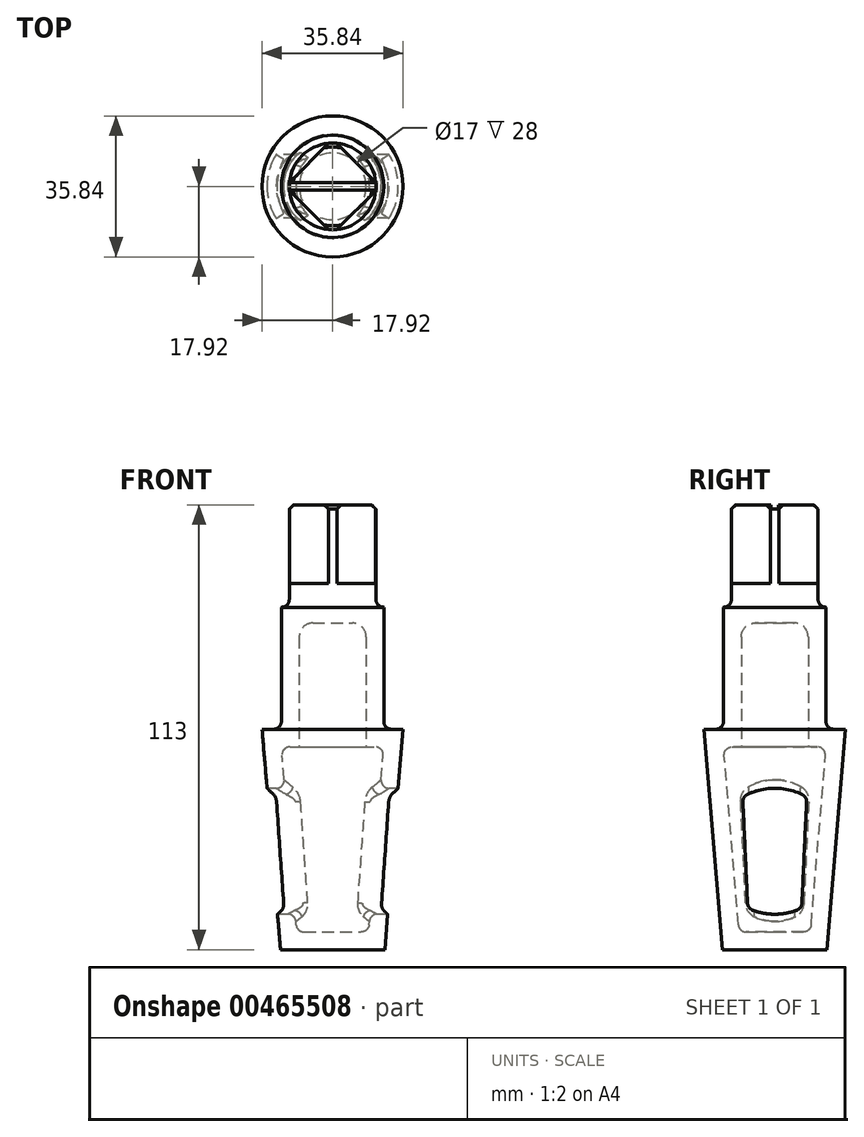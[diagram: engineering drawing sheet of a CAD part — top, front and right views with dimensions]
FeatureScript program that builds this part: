
annotation { "Feature Type Name" : "Feature", "Feature Type Description" : "" }
export const myFeature = defineFeature(function(context is Context, id is Id, definition is map)
    precondition{}
    {
        {
            var Q0;
            Q0=qCreatedBy(makeId("Front.planeOp"),FACE);
            var sketch = newSketch(context, id + "F0", { "sketchPlane" : qUnion([Q0])});
            skLineSegment(sketch, "E0", {"start": v(0, -32.47) * mm, "end": v(0, 104.3) * mm, "construction": true});
            skLineSegment(sketch, "E1", {"start": v(0, -25) * mm, "end": v(13.25, -25) * mm});
            skLineSegment(sketch, "E2", {"start": v(13.25, -25) * mm, "end": v(17.92, 31) * mm});
            skLineSegment(sketch, "E3", {"start": v(17.92, 31) * mm, "end": v(13, 31) * mm});
            skLineSegment(sketch, "E4", {"start": v(13, 31) * mm, "end": v(13, 62) * mm});
            skLineSegment(sketch, "E5", {"start": v(13, 62) * mm, "end": v(11, 62) * mm});
            skLineSegment(sketch, "E6", {"start": v(11, 62) * mm, "end": v(11, 88) * mm});
            skLineSegment(sketch, "E7", {"start": v(11, 88) * mm, "end": v(0, 88) * mm});
            skLineSegment(sketch, "E8", {"start": v(0, 88) * mm, "end": v(0, -25) * mm});
            skLineSegment(sketch, "E9.0", {"start": v(8.5, 26.5) * mm, "end": v(8.5, 54.5) * mm});
            skLineSegment(sketch, "E9.1", {"start": v(10.85, 26.5) * mm, "end": v(8.5, 26.5) * mm});
            skLineSegment(sketch, "E9.2", {"start": v(9.26, -18.67) * mm, "end": v(12.85, 24.33) * mm});
            skLineSegment(sketch, "E9.3", {"start": v(0, -20.5) * mm, "end": v(7.27, -20.5) * mm});
            skLineSegment(sketch, "E10", {"start": v(0, 58) * mm, "end": v(5, 58) * mm});
            skPoint(sketch, "E11.visualSharp", {"position": v(8.5, 58) * mm});
            skArc(sketch, "E11.filletArc", {"start": v(8.5, 54.5) * mm, "mid": v(7.47, 56.97) * mm, "end": v(5, 58) * mm});
            skPoint(sketch, "E12.visualSharp", {"position": v(13.03, 26.5) * mm});
            skArc(sketch, "E12.filletArc", {"start": v(12.85, 24.33) * mm, "mid": v(12.32, 25.85) * mm, "end": v(10.85, 26.5) * mm});
            skPoint(sketch, "E13.visualSharp", {"position": v(9.1, -20.5) * mm});
            skArc(sketch, "E13.filletArc", {"start": v(7.27, -20.5) * mm, "mid": v(8.62, -19.97) * mm, "end": v(9.26, -18.67) * mm});
            skSolve(sketch);
        }
        {
            var Q0;
            {var subQ1=sQuery(id+"F0.wireOp",EDGE,"E1");Q0=makeQuery(id+"F0.imprint","IMPRINT",FACE,{"disambiguationData":[TD([[makeQuery(id+"F0.imprint","IMPRINT",EDGE,{"derivedFrom":subQ1}),1.0]])]});}
            var Q1;
            Q1=sQuery(id+"F0.wireOp",EDGE,"E0");
            revolve(context, id + "F1", {"entities" : qUnion([Q0]), "axis" : qUnion([Q1]), "revolveType" : RevolveType.FULL});
        }
        {
            var Q0;
            Q0=qCreatedBy(makeId("Right.planeOp"),FACE);
            var sketch = newSketch(context, id + "F2", { "sketchPlane" : qUnion([Q0])});
            skArc(sketch, "E14", {"start": v(6.96, 14.4) * mm, "mid": v(0, 16) * mm, "end": v(-6.96, 14.4) * mm});
            skLineSegment(sketch, "E15", {"start": v(0, 0) * mm, "end": v(0, -8.72) * mm, "construction": true});
            skLineSegment(sketch, "E16", {"start": v(8.1, 12.51) * mm, "end": v(6.9, -13.2) * mm});
            skLineSegment(sketch, "E17.MirrorCS", {"start": v(-8.1, 12.51) * mm, "end": v(-6.9, -13.2) * mm});
            skPoint(sketch, "E18.orphan", {"position": v(8.34, 17.9) * mm});
            skPoint(sketch, "E19.orphan", {"position": v(-8.34, 17.9) * mm});
            skPoint(sketch, "E20.orphan", {"position": v(-6.6, -19.71) * mm});
            skPoint(sketch, "E21.orphan", {"position": v(6.6, -19.71) * mm});
            skArc(sketch, "E22.trimOffspring", {"start": v(-5.61, -14.98) * mm, "mid": v(0, -16) * mm, "end": v(5.61, -14.98) * mm});
            skPoint(sketch, "E23.visualSharp", {"position": v(8.15, 13.77) * mm});
            skArc(sketch, "E23.filletArc", {"start": v(8.1, 12.51) * mm, "mid": v(7.81, 13.63) * mm, "end": v(6.96, 14.4) * mm});
            skPoint(sketch, "E24.visualSharp", {"position": v(-8.15, 13.77) * mm});
            skArc(sketch, "E24.filletArc", {"start": v(-6.96, 14.4) * mm, "mid": v(-7.81, 13.63) * mm, "end": v(-8.1, 12.51) * mm});
            skPoint(sketch, "E25.visualSharp", {"position": v(-6.85, -14.46) * mm});
            skArc(sketch, "E25.filletArc", {"start": v(-6.9, -13.2) * mm, "mid": v(-6.53, -14.29) * mm, "end": v(-5.61, -14.98) * mm});
            skPoint(sketch, "E26.visualSharp", {"position": v(6.85, -14.46) * mm});
            skArc(sketch, "E26.filletArc", {"start": v(5.61, -14.98) * mm, "mid": v(6.53, -14.29) * mm, "end": v(6.9, -13.2) * mm});
            skSolve(sketch);
        }
        {
            var Q0;
            Q0 = qSketchRegion(id + "F2", true);
            extrude(context, id + "F3", {"entities" : qUnion([Q0]), "operationType" : NewBodyOperationType.REMOVE, "depth" : 40 * mm, "symmetric" : true});
        }
        {
            var Q0;
            Q0=makeQuery(id+"F1.opRevolve","SWEPT_EDGE",EDGE,{"disambiguationData":[OSD([sQuery(id+"F0.wireOp",EDGE,"E6"),sQuery(id+"F0.wireOp",EDGE,"E7")])]});
            chamfer(context, id + "F4", {"entities" : qUnion([Q0]), "width" : 1 * mm, "tangentPropagation" : true});
        }
        {
            var Q0;
            Q0=makeQuery(id+"F1.opRevolve","SWEPT_FACE",FACE,{"disambiguationData":[OSD([sQuery(id+"F0.wireOp",EDGE,"E7")])]});
            var sketch = newSketch(context, id + "F5", { "sketchPlane" : qUnion([Q0])});
            skCircle(sketch, "E27.cCircle", {"center": v(0, 0) * mm, "radius": 12.02 * mm, "construction": true});
            skLineSegment(sketch, "E27.0", {"start": v(0, 12.02) * mm, "end": v(12.02, 0) * mm});
            skLineSegment(sketch, "E27.1", {"start": v(12.02, 0) * mm, "end": v(0, -12.02) * mm});
            skLineSegment(sketch, "E27.2", {"start": v(0, -12.02) * mm, "end": v(-12.02, 0) * mm});
            skLineSegment(sketch, "E27.3", {"start": v(-12.02, 0) * mm, "end": v(0, 12.02) * mm});
            skCircle(sketch, "E28.0", {"center": v(0, 0) * mm, "radius": 11 * mm});
            skSolve(sketch);
        }
        {
            var Q0;
            {var subQ0=sQuery(id+"F5.wireOp",EDGE,"E27.3");var subQ1=sQuery(id+"F0.wireOp",EDGE,"E7");var subQ2=makeQuery(id+"F4.opChamfer","BLEND_EDGE",EDGE,{"blendedFrom":[makeQuery(id+"F1.opRevolve","SWEPT_EDGE",EDGE,{"disambiguationData":[OSD([sQuery(id+"F0.wireOp",EDGE,"E6"),subQ1])]}),makeQuery(id+"F1.opRevolve","SWEPT_FACE",FACE,{"disambiguationData":[OSD([subQ1])]})],"blendedInto":[makeQuery(id+"F1.opRevolve","SWEPT_FACE",FACE,{"disambiguationData":[OSD([subQ1])]})]});var subQ3=makeQuery(id+"F5.imprint","INTERSECT",VERTEX,{"disambiguationData":[OD(0.0)],"derivedFrom":[subQ2,subQ0]});Q0=makeQuery(id+"F5.imprint","IMPRINT",FACE,{"disambiguationData":[TD([[makeQuery(id+"F5.imprint","IMPRINT",EDGE,{"disambiguationData":[TD([[subQ3,-1.0]])],"derivedFrom":subQ0}),1.0]])]});}
            var Q1;
            {var subQ0=sQuery(id+"F5.wireOp",EDGE,"E28.0");var subQ1=sQuery(id+"F5.wireOp",EDGE,"E27.3");var subQ2=makeQuery(id+"F5.imprint","INTERSECT",VERTEX,{"disambiguationData":[OD(0.0)],"derivedFrom":[subQ1,subQ0]});Q1=makeQuery(id+"F5.imprint","IMPRINT",FACE,{"disambiguationData":[TD([[makeQuery(id+"F5.imprint","IMPRINT",EDGE,{"disambiguationData":[TD([[subQ2,1.0]])],"derivedFrom":subQ0}),1.0]])]});}
            var Q2;
            {var subQ0=sQuery(id+"F5.wireOp",EDGE,"E27.2");var subQ1=sQuery(id+"F0.wireOp",EDGE,"E7");var subQ2=makeQuery(id+"F4.opChamfer","BLEND_EDGE",EDGE,{"blendedFrom":[makeQuery(id+"F1.opRevolve","SWEPT_EDGE",EDGE,{"disambiguationData":[OSD([sQuery(id+"F0.wireOp",EDGE,"E6"),subQ1])]}),makeQuery(id+"F1.opRevolve","SWEPT_FACE",FACE,{"disambiguationData":[OSD([subQ1])]})],"blendedInto":[makeQuery(id+"F1.opRevolve","SWEPT_FACE",FACE,{"disambiguationData":[OSD([subQ1])]})]});var subQ3=makeQuery(id+"F5.imprint","INTERSECT",VERTEX,{"disambiguationData":[OD(0.0)],"derivedFrom":[subQ2,subQ0]});Q2=makeQuery(id+"F5.imprint","IMPRINT",FACE,{"disambiguationData":[TD([[makeQuery(id+"F5.imprint","IMPRINT",EDGE,{"disambiguationData":[TD([[subQ3,-1.0]])],"derivedFrom":subQ0}),1.0]])]});}
            var Q3;
            {var subQ0=sQuery(id+"F5.wireOp",EDGE,"E28.0");var subQ1=sQuery(id+"F5.wireOp",EDGE,"E27.2");var subQ2=makeQuery(id+"F5.imprint","INTERSECT",VERTEX,{"disambiguationData":[OD(0.0)],"derivedFrom":[subQ1,subQ0]});Q3=makeQuery(id+"F5.imprint","IMPRINT",FACE,{"disambiguationData":[TD([[makeQuery(id+"F5.imprint","IMPRINT",EDGE,{"disambiguationData":[TD([[subQ2,1.0]])],"derivedFrom":subQ0}),1.0]])]});}
            var Q4;
            {var subQ0=sQuery(id+"F5.wireOp",EDGE,"E28.0");var subQ1=sQuery(id+"F5.wireOp",EDGE,"E27.1");var subQ2=makeQuery(id+"F5.imprint","INTERSECT",VERTEX,{"disambiguationData":[OD(0.0)],"derivedFrom":[subQ1,subQ0]});Q4=makeQuery(id+"F5.imprint","IMPRINT",FACE,{"disambiguationData":[TD([[makeQuery(id+"F5.imprint","IMPRINT",EDGE,{"disambiguationData":[TD([[subQ2,1.0]])],"derivedFrom":subQ0}),1.0]])]});}
            var Q5;
            {var subQ0=sQuery(id+"F5.wireOp",EDGE,"E27.1");var subQ1=sQuery(id+"F0.wireOp",EDGE,"E7");var subQ2=makeQuery(id+"F4.opChamfer","BLEND_EDGE",EDGE,{"blendedFrom":[makeQuery(id+"F1.opRevolve","SWEPT_EDGE",EDGE,{"disambiguationData":[OSD([sQuery(id+"F0.wireOp",EDGE,"E6"),subQ1])]}),makeQuery(id+"F1.opRevolve","SWEPT_FACE",FACE,{"disambiguationData":[OSD([subQ1])]})],"blendedInto":[makeQuery(id+"F1.opRevolve","SWEPT_FACE",FACE,{"disambiguationData":[OSD([subQ1])]})]});var subQ3=makeQuery(id+"F5.imprint","INTERSECT",VERTEX,{"disambiguationData":[OD(0.0)],"derivedFrom":[subQ2,subQ0]});Q5=makeQuery(id+"F5.imprint","IMPRINT",FACE,{"disambiguationData":[TD([[makeQuery(id+"F5.imprint","IMPRINT",EDGE,{"disambiguationData":[TD([[subQ3,-1.0]])],"derivedFrom":subQ0}),1.0]])]});}
            var Q6;
            {var subQ0=sQuery(id+"F5.wireOp",EDGE,"E27.0");var subQ1=sQuery(id+"F0.wireOp",EDGE,"E7");var subQ2=makeQuery(id+"F4.opChamfer","BLEND_EDGE",EDGE,{"blendedFrom":[makeQuery(id+"F1.opRevolve","SWEPT_EDGE",EDGE,{"disambiguationData":[OSD([sQuery(id+"F0.wireOp",EDGE,"E6"),subQ1])]}),makeQuery(id+"F1.opRevolve","SWEPT_FACE",FACE,{"disambiguationData":[OSD([subQ1])]})],"blendedInto":[makeQuery(id+"F1.opRevolve","SWEPT_FACE",FACE,{"disambiguationData":[OSD([subQ1])]})]});var subQ3=makeQuery(id+"F5.imprint","INTERSECT",VERTEX,{"disambiguationData":[OD(0.0)],"derivedFrom":[subQ2,subQ0]});Q6=makeQuery(id+"F5.imprint","IMPRINT",FACE,{"disambiguationData":[TD([[makeQuery(id+"F5.imprint","IMPRINT",EDGE,{"disambiguationData":[TD([[subQ3,-1.0]])],"derivedFrom":subQ0}),1.0]])]});}
            var Q7;
            {var subQ0=sQuery(id+"F5.wireOp",EDGE,"E28.0");var subQ1=sQuery(id+"F5.wireOp",EDGE,"E27.0");var subQ2=makeQuery(id+"F5.imprint","INTERSECT",VERTEX,{"disambiguationData":[OD(0.0)],"derivedFrom":[subQ1,subQ0]});Q7=makeQuery(id+"F5.imprint","IMPRINT",FACE,{"disambiguationData":[TD([[makeQuery(id+"F5.imprint","IMPRINT",EDGE,{"disambiguationData":[TD([[subQ2,1.0]])],"derivedFrom":subQ0}),1.0]])]});}
            extrude(context, id + "F6", {"entities" : qUnion([Q0, Q1, Q2, Q3, Q4, Q5, Q6, Q7]), "operationType" : NewBodyOperationType.REMOVE, "oppositeDirection" : true, "depth" : 20 * mm});
        }
        {
            var Q0;
            Q0=makeQuery(id+"F1.opRevolve","SWEPT_FACE",FACE,{"disambiguationData":[OSD([sQuery(id+"F0.wireOp",EDGE,"E7")])]});
            var sketch = newSketch(context, id + "F7", { "sketchPlane" : qUnion([Q0])});
            skLineSegment(sketch, "E29.bottom", {"start": v(-12.5, 1) * mm, "end": v(12.5, 1) * mm});
            skLineSegment(sketch, "E29.top", {"start": v(-12.5, -1) * mm, "end": v(12.5, -1) * mm});
            skLineSegment(sketch, "E29.left", {"start": v(-12.5, 1) * mm, "end": v(-12.5, -1) * mm});
            skLineSegment(sketch, "E29.right", {"start": v(12.5, 1) * mm, "end": v(12.5, -1) * mm});
            skPoint(sketch, "E29.middle", {"position": v(0, 0) * mm});
            skSolve(sketch);
        }
        {
            var Q0;
            Q0 = qSketchRegion(id + "F7", true);
            extrude(context, id + "F8", {"entities" : qUnion([Q0]), "operationType" : NewBodyOperationType.REMOVE, "oppositeDirection" : true, "depth" : 1 * mm});
        }
        {
            var Q0;
            Q0=makeQuery(id+"F1.opRevolve","SWEPT_EDGE",EDGE,{"disambiguationData":[OSD([sQuery(id+"F0.wireOp",EDGE,"E5"),sQuery(id+"F0.wireOp",EDGE,"E6")])]});
            var Q1;
            Q1=makeQuery(id+"F1.opRevolve","SWEPT_EDGE",EDGE,{"disambiguationData":[OSD([sQuery(id+"F0.wireOp",EDGE,"E3"),sQuery(id+"F0.wireOp",EDGE,"E4")])]});
            var Q2;
            Q2=makeQuery(id+"F3.boolean.opBoolean","INTERSECT",EDGE,{"disambiguationData":[OD(0.0)],"derivedFrom":[makeQuery(id+"F1.opRevolve","SWEPT_FACE",FACE,{"disambiguationData":[OSD([sQuery(id+"F0.wireOp",EDGE,"E9.2")])]}),makeQuery(id+"F3.opExtrude","SWEPT_FACE",FACE,{"disambiguationData":[OSD([sQuery(id+"F2.wireOp",EDGE,"E16")])]})]});
            var Q3;
            Q3=makeQuery(id+"F3.boolean.opBoolean","INTERSECT",EDGE,{"disambiguationData":[OD(1.0)],"derivedFrom":[makeQuery(id+"F1.opRevolve","SWEPT_FACE",FACE,{"disambiguationData":[OSD([sQuery(id+"F0.wireOp",EDGE,"E9.2")])]}),makeQuery(id+"F3.opExtrude","SWEPT_FACE",FACE,{"disambiguationData":[OSD([sQuery(id+"F2.wireOp",EDGE,"E16")])]})]});
            fillet(context, id + "F9", {"entities" : qUnion([Q0, Q1, Q2, Q3]), "radius" : 2 * mm, "tangentPropagation" : true, "allowEdgeOverflow" : false});
        }
    });
